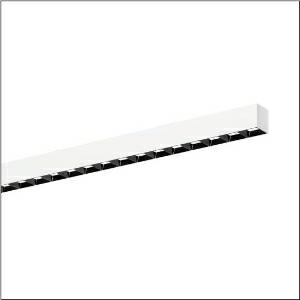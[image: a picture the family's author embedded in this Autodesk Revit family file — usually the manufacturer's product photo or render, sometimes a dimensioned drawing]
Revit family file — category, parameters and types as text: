
# Revit family: silica_r__21_51mx21tat4w_a490
name_source: partatom
category: Lighting Fixtures
units: mm (PartAtom-declared; Revit-internal decimal feet)

## family parameters
Cut with Voids When Loaded = No
Host = Face
Light Source = No
Part Type = Normal
Room Calculation Point = No
Round Connector Dimension = Use Diameter
Shared = No

## types (1)
- --- (1 x LED, 3720 lm, 32.2 W, 6500K)
    Apparent Load = 32 VA
    CIE Flux Codes = 85 99 100 100 100
    Color Rendering = 80
    Color Temperature = 6500K
    Default Elevation = 1800 mm
    Description = Silica® 21, office luminaire, primary light control with darklight reflector, of PMMA, black, CAT 2 (L<= 3000cd/m²), light emission: direct distribution, primary light characteristic: symmetric, installation type: surface-mounted, LED, rated luminous flux: 3.720lm, luminous efficacy: 110lm/W, light colour: 8tw, colour temperature: 2700..6500K, control gear: ECG DALI, with terminal, 3+2-pole, max. 2.5mm², mains connection: 220..240V, AC, 50/60Hz, rated input power: 33.8W, luminaire housing, of aluminium, traffic white (RAL 9016), length: 1.204mm, width: 53mm, height: 53mm, protection rating (complete): IP20, insulation class (complete): insulation class I (protective earthing), certification: CE, permissible operating ambient temperature: 0..+35°C, standard: EN 50419, packaging unit: 1 piece
    Height = 53 mm
    Lamp = 1 x LED
    Lamp Light Flux = 3720 lm
    Lamp Power = 32.2 W
    Lamp count = 1
    Length = 1204 mm
    Luminous efficacy = 116 lm/W
    Manufacturer = Siteco
    ModVariant = No
    Model = 51MX21TAT4W
    Mounting Place = Ceiling
    Mounting Type = Surface mounted
    Number of Poles = 1
    OnlyDefault = Yes
    Power Factor = 1
    Product Name = Silica® 21
    Product group = office luminaire | ceiling mounted
    ProductGroupID = 302
    Protection Class = Protection class I
    Protection Degree = IP 20
    RLX_Detail_Level = 1
    RlxData = <blob elided: 37937 chars, md5=023b642e>
    Socket = socket
    Standby Power = 0 W
    System Light Flux = 3720 lm
    System Power = 32 W
    Type Comments = individual setting
    Type Image = l_1251676.jpg
    URL = http://relux.com
    VarID = @adj_046179
    Voltage = 0 V
    Weight = 0.00 kg
    Width = 53 mm

## geometry (parser evidence)
native form markers: Blend x4, Sweep x9
no freeform markers — native parametric forms only
